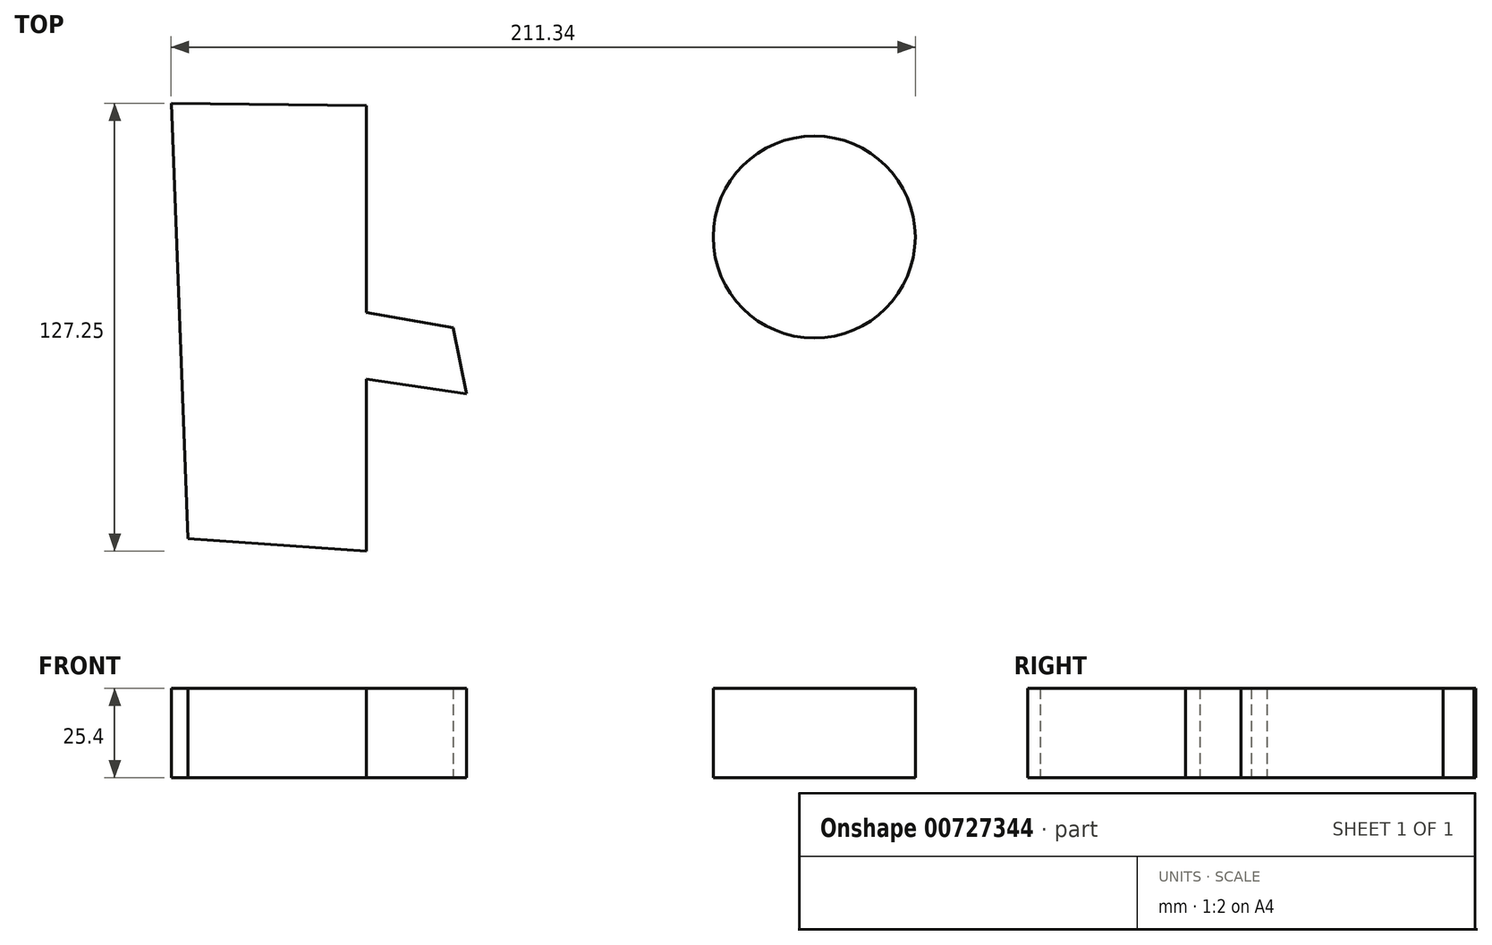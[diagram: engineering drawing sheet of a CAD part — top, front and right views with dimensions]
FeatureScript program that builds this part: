
annotation { "Feature Type Name" : "Feature", "Feature Type Description" : "" }
export const myFeature = defineFeature(function(context is Context, id is Id, definition is map)
    precondition{}
    {
        {
            var Q0;
            Q0=qCreatedBy(makeId("Top.planeOp"),FACE);
            var sketch = newSketch(context, id + "F0", { "sketchPlane" : qUnion([Q0])});
            skLineSegment(sketch, "E0", {"start": v(-143.86, 59.4) * mm, "end": v(-139.1, -64.34) * mm});
            skLineSegment(sketch, "E1", {"start": v(-139.1, -64.34) * mm, "end": v(-88.46, -67.85) * mm});
            skLineSegment(sketch, "E2", {"start": v(-88.46, -67.85) * mm, "end": v(-88.46, -19) * mm});
            skLineSegment(sketch, "E3", {"start": v(-88.46, -19) * mm, "end": v(-59.91, -23.14) * mm});
            skLineSegment(sketch, "E4", {"start": v(-59.91, -23.14) * mm, "end": v(-63.76, -4.36) * mm});
            skLineSegment(sketch, "E5", {"start": v(-63.76, -4.36) * mm, "end": v(-88.46, 0) * mm});
            skLineSegment(sketch, "E6", {"start": v(-88.46, 0) * mm, "end": v(-88.46, 58.77) * mm});
            skLineSegment(sketch, "E7", {"start": v(-88.46, 58.77) * mm, "end": v(-143.86, 59.4) * mm});
            skSolve(sketch);
        }
        {
            var Q0;
            Q0 = qSketchRegion(id + "F0", true);
            extrude(context, id + "F1", {"entities" : qUnion([Q0]), "depth" : 25.4 * mm, "offsetDistance" : 25.4 * mm});
        }
        {
            var Q0;
            Q0=qCreatedBy(makeId("Top.planeOp"),FACE);
            var sketch = newSketch(context, id + "F2", { "sketchPlane" : qUnion([Q0])});
            skCircle(sketch, "E8", {"center": v(38.78, 21.4) * mm, "radius": 28.7 * mm});
            skSolve(sketch);
        }
        {
            var Q0;
            Q0 = qSketchRegion(id + "F2", true);
            extrude(context, id + "F3", {"entities" : qUnion([Q0]), "depth" : 25.4 * mm, "offsetDistance" : 25.4 * mm});
        }
    });
